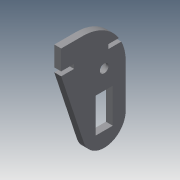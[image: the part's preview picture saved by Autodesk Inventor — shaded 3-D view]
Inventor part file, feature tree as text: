
AUTODESK INVENTOR PART (.ipt)
format: ipt  version: 2013 (Build 170138000, 138)  size: 392,704 bytes
history: native  units: mm
features: sketch x33, extrude x28
ambient origin geometry x8: Origin, YZ Plane, XZ Plane, XY Plane, X Axis, Y Axis, Z Axis, Center Point
bodies: Solid1 (feature_tree)
feature tree (61):
  extrude  "Extrusion1"  Depth=66.3mm
  extrude  "Extrusion2"  Depth=55.0mm
  extrude  "Extrusion3"  Depth=55.0mm
  extrude  "Extrusion4"  Depth=9.9mm
  extrude  "Extrusion5"  Depth=9.9mm
  extrude  "Extrusion6"  Depth=3.0mm
  extrude  "Extrusion7"  Depth=3.0mm
  extrude  "Extrusion8"  Depth=13.6mm
  extrude  "Extrusion9"  Depth=45.0mm
  sketch  "Sketch10"  dims[d22=15.0mm d23=5.0mm d24=0.0mm]
  extrude  "Extrusion10"  Depth=5.0mm TaperAngle=0.0deg
  extrude  "Extrusion11"  Depth=55.0mm
  extrude  "Extrusion12"  Depth=20.0mm
  sketch  "Sketch14"  dims[d33=10.0mm d34=32.9mm d35=0.0mm]
  extrude  "Extrusion13"  Depth=5.0mm TaperAngle=0.0deg
  extrude  "Extrusion14"  Depth=32.9mm TaperAngle=0.0deg
  extrude  "Extrusion15"  Depth=25.0mm
  extrude  "Extrusion16"  Depth=5.0mm TaperAngle=0.0deg
  extrude  "Extrusion17"  Depth=15.0mm
  sketch  "Sketch20"  dims[d50=28.0mm d51=5.0mm d52=0.0mm]
  extrude  "Extrusion18"  Depth=18.0mm
  extrude  "Extrusion19"  Depth=32.9mm TaperAngle=0.0deg
  extrude  "Extrusion20"  Depth=5.0mm TaperAngle=0.0deg
  extrude  "Extrusion21"  Depth=5.0mm
  extrude  "Extrusion22"  Depth=13.6mm
  extrude  "Extrusion23"  Depth=12.5mm
  sketch  "Sketch27"  dims[d68=21.4mm d69=2.0mm]
  extrude  "Extrusion24"  Depth=12.2mm
  extrude  "Extrusion25"  Depth=5.0mm TaperAngle=0.0deg
  extrude  "Extrusion26"  Depth=2.0mm
  sketch  "Sketch31"  dims[d76=21.4mm]
  extrude  "Extrusion27"  Depth=2.0mm
  extrude  "Extrusion28"  Depth=2.05mm
  sketch  "Sketch1"  dims[d0=33.15mm d2=66.3mm]
  sketch  "Sketch2"  dims[d4=18.1mm d5=55.0mm]
  sketch  "Sketch3"  dims[d6=20.0mm d7=55.0mm]
  sketch  "Sketch4"  dims[d8=40.2mm d9=9.9mm]
  sketch  "Sketch5"  dims[d10=9.5mm d11=9.9mm]
  sketch  "Sketch6"  dims[d12=9.5mm d13=3.0mm]
  sketch  "Sketch7"  dims[d14=3.0mm d15=3.0mm]
  sketch  "Sketch8"  dims[d16=3.0mm d17=13.6mm]
  sketch  "Sketch9"  dims[d20=25.0mm d21=45.0mm]
  sketch  "Sketch11"  dims[d25=18.1mm d26=55.0mm]
  sketch  "Sketch12"  dims[d27=40.2mm d28=20.0mm]
  sketch  "Sketch13"  dims[d29=5.0mm d30=0.0mm d31=5.0mm d32=0.0mm]
  sketch  "Sketch15"  dims[d36=25.0mm d37=0.0mm d38=25.0mm]
  sketch  "Sketch16"  dims[d39=10.0mm d40=5.0mm d41=0.0mm]
  sketch  "Sketch17"  dims[d42=12.5mm d43=15.0mm]
  sketch  "Sketch18"  dims[d44=10.0mm d45=0.0mm d46=18.0mm]
  sketch  "Sketch19"  dims[d47=5.0mm d48=32.9mm d49=0.0mm]
  sketch  "Sketch21"  dims[d53=10.0mm d54=0.0mm d55=5.0mm]
  sketch  "Sketch22"  dims[d56=12.5mm d57=13.6mm]
  sketch  "Sketch23"  dims[d58=10.0mm d59=0.0mm d60=12.5mm]
  sketch  "Sketch24"  dims[d61=12.4mm d62=12.2mm]
  sketch  "Sketch25"  dims[d63=6.2mm d64=5.0mm d65=0.0mm]
  sketch  "Sketch26"  dims[d66=10.6mm d67=2.0mm]
  sketch  "Sketch28"  dims[d70=5.0mm d71=0.0mm d72=2.05mm]
  sketch  "Sketch29"  dims[d73=2.05mm]
  sketch  "Sketch30"  dims[d74=5.0mm d75=0.0mm]
  sketch  "Sketch32"  dims[d77=2.05mm]
  sketch  "Sketch33"  dims[d78=2.0mm d79=10.6mm d80=2.05mm d81=2.0mm d82=5.0mm d83=0.0mm d84=45.0mm d86=5.0mm d87=5.0mm d88=39.0mm d89=0.0mm d90=22.0mm d91=5.0mm d92=0.0mm d93=3.0mm d94=0.0mm d95=10.0mm d96=2.0mm d97=0.0mm d98=2.0mm d99=0.0mm d100=10.25mm d101=7.25mm d102=22.0mm d103=0.0mm d104=10.0mm d105=2.0mm d106=0.0mm d107=10.0mm d108=3.0mm d109=0.0mm d111=14.0mm d112=14.0mm d113=5.0mm d114=0.0mm d115=15.0mm d116=15.0mm d117=37.9mm d118=0.0mm d119=29.9mm d120=0.0mm d121=29.9mm d122=0.0mm d123=29.9mm d124=0.0mm]
